# Revit family: Cumberland-Elle Lounge_Sofa1
name_source: partatom
category: Furniture
revit_build: Autodesk Revit 2014 (Build: 20130308_1515(x64)
units: mm (PartAtom-declared; Revit-internal decimal feet)

## types (3) — shared parameters
Assembly Code = E2020200
Base Finish = CUM - Stainless - Steel
Depth = 27 9/32"
Height = 28 15/16"
Keynote = 12500
Low Emitting Finish = Yes
Low Emitting Material = Yes
Manufacturer = Cumberland
Pad Finish = CUM - Linen - Beige
Salvage or Reuse = Yes
Seat Finish = CUM - Linen - Beige
Type Comments = Elle Lounge
URL = www.cumberlandfurniture.com
zero-valued in all types: Percentage of Recycled Content

## per-type parameters (varying)
| type | Description | Width |
| 2440 | Elle Lounge 33"W 28"H 27"D Lounge Chair | 33 3/32" |
| 2441 | Elle Lounge 66"W 28"H 27"D | 66" |
| 2443 | Elle Lounge 33"W 28"H 27"D Swivel Chair | 33 3/32" |

note: column(s) folded — value = type name in every type: Model

## geometry (parser evidence)
native form markers: Sweep x4
no freeform markers — native parametric forms only
